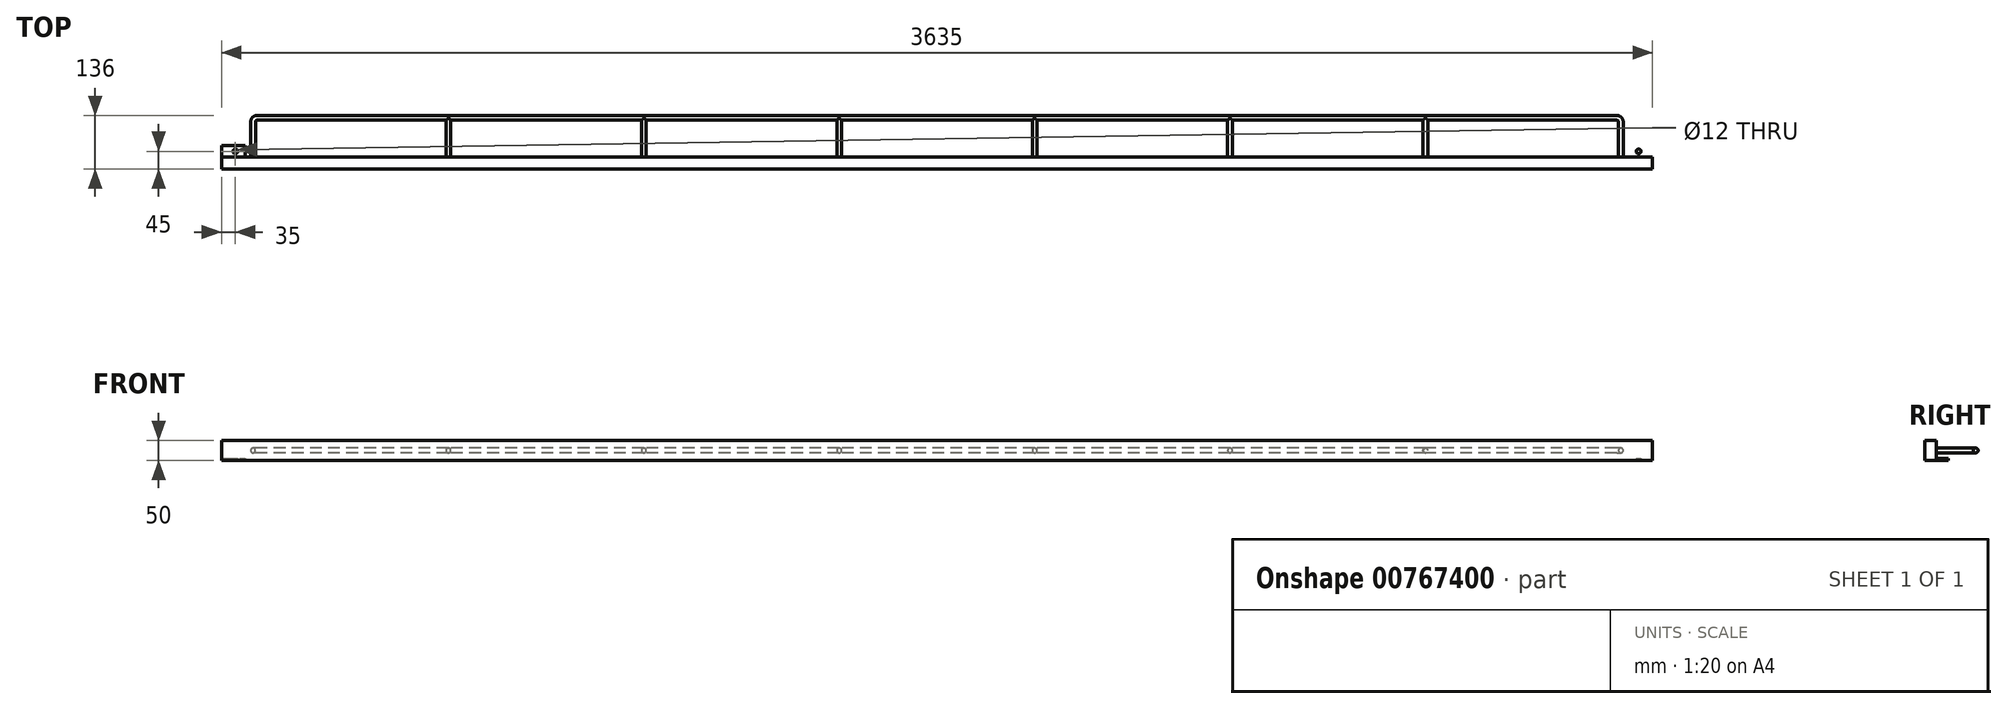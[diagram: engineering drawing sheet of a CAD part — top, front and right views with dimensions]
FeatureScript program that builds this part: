
annotation { "Feature Type Name" : "Feature", "Feature Type Description" : "" }
export const myFeature = defineFeature(function(context is Context, id is Id, definition is map)
    precondition{}
    {
        {
            var Q0;
            Q0=qCreatedBy(makeId("Front.planeOp"),FACE);
            var sketch = newSketch(context, id + "F0", { "sketchPlane" : qUnion([Q0])});
            skLineSegment(sketch, "E0.bottom", {"start": v(1817.5, -25) * mm, "end": v(-1817.5, -25) * mm});
            skLineSegment(sketch, "E0.top", {"start": v(1817.5, 25) * mm, "end": v(-1817.5, 25) * mm});
            skLineSegment(sketch, "E0.left", {"start": v(1817.5, -25) * mm, "end": v(1817.5, 25) * mm});
            skLineSegment(sketch, "E0.right", {"start": v(-1817.5, -25) * mm, "end": v(-1817.5, 25) * mm});
            skPoint(sketch, "E0.middle", {"position": v(0, 0) * mm});
            skSolve(sketch);
        }
        {
            var Q0;
            Q0=qSketchRegion(id+"F0",true);
            extrude(context, id + "F1", {"entities" : qUnion([Q0]), "depth" : 15 * mm, "offsetDistance" : 25 * mm, "hasSecondDirection" : true, "secondDirectionOppositeDirection" : true, "secondDirectionDepth" : 15 * mm});
        }
        {
            var Q0;
            Q0=makeQuery(id+"F1.opExtrude","SWEPT_FACE",FACE,{"disambiguationData":[OSD([sQuery(id+"F0.wireOp",EDGE,"E0.bottom")])]});
            var sketch = newSketch(context, id + "F2", { "sketchPlane" : qUnion([Q0])});
            skLineSegment(sketch, "E1.0", {"start": v(-1817.5, 15) * mm, "end": v(-1817.5, -15) * mm});
            skLineSegment(sketch, "E2.bottom", {"start": v(-1817.5, -15) * mm, "end": v(-1757.5, -15) * mm});
            skLineSegment(sketch, "E2.top", {"start": v(-1817.5, 45) * mm, "end": v(-1757.5, 45) * mm});
            skLineSegment(sketch, "E2.left", {"start": v(-1817.5, -15) * mm, "end": v(-1817.5, 45) * mm});
            skLineSegment(sketch, "E2.right", {"start": v(-1757.5, -15) * mm, "end": v(-1757.5, 45) * mm});
            skLineSegment(sketch, "E3", {"start": v(-1817.5, 0) * mm, "end": v(-1773.05, 0) * mm});
            skLineSegment(sketch, "E4.MirrorCS", {"start": v(-1817.5, -15) * mm, "end": v(-1817.5, 15) * mm});
            skLineSegment(sketch, "E5.MirrorCS", {"start": v(-1817.5, 15) * mm, "end": v(-1817.5, -45) * mm});
            skLineSegment(sketch, "E6.MirrorCS", {"start": v(-1817.5, -45) * mm, "end": v(-1757.5, -45) * mm});
            skLineSegment(sketch, "E7.MirrorCS", {"start": v(-1757.5, 15) * mm, "end": v(-1757.5, -45) * mm});
            skSolve(sketch);
        }
        {
            var Q0;
            {var subQ0=sQuery(id+"F2.wireOp",EDGE,"E2.bottom");Q0=makeQuery(id+"F2.imprint","IMPRINT",FACE,{"disambiguationData":[TD([[makeQuery(id+"F2.imprint","IMPRINT",EDGE,{"derivedFrom":subQ0}),1.0]])]});}
            var Q1;
            {var subQ1=sQuery(id+"F2.wireOp",EDGE,"E2.bottom");Q1=makeQuery(id+"F2.imprint","IMPRINT",FACE,{"disambiguationData":[TD([[makeQuery(id+"F2.imprint","IMPRINT",EDGE,{"derivedFrom":subQ1}),-1.0]])]});}
            extrude(context, id + "F3", {"entities" : qUnion([Q0, Q1]), "operationType" : NewBodyOperationType.ADD, "depth" : 5 * mm, "offsetDistance" : 25 * mm});
        }
        {
            var Q0;
            Q0=makeQuery(id+"F1.opExtrude","SWEPT_FACE",FACE,{"disambiguationData":[OSD([sQuery(id+"F0.wireOp",EDGE,"E0.bottom")])]});
            var sketch = newSketch(context, id + "F4", { "sketchPlane" : qUnion([Q0])});
            skLineSegment(sketch, "E8.0", {"start": v(1817.5, 15) * mm, "end": v(1817.5, -15) * mm});
            skLineSegment(sketch, "E9.bottom", {"start": v(1817.5, -15) * mm, "end": v(1757.5, -15) * mm});
            skLineSegment(sketch, "E9.top", {"start": v(1817.5, 45) * mm, "end": v(1757.5, 45) * mm});
            skLineSegment(sketch, "E9.left", {"start": v(1817.5, -15) * mm, "end": v(1817.5, 45) * mm});
            skLineSegment(sketch, "E9.right", {"start": v(1757.5, -15) * mm, "end": v(1757.5, 45) * mm});
            skLineSegment(sketch, "E10", {"start": v(1817.5, 0) * mm, "end": v(1727.5, 0) * mm});
            skLineSegment(sketch, "E11.MirrorCS", {"start": v(1817.5, 15) * mm, "end": v(1817.5, -45) * mm});
            skLineSegment(sketch, "E12.MirrorCS", {"start": v(1817.5, -45) * mm, "end": v(1757.5, -45) * mm});
            skLineSegment(sketch, "E13.MirrorCS", {"start": v(1757.5, 15) * mm, "end": v(1757.5, -45) * mm});
            skSolve(sketch);
        }
        {
            var Q0;
            {var subQ0=sQuery(id+"F4.wireOp",EDGE,"E9.bottom");Q0=makeQuery(id+"F4.imprint","IMPRINT",FACE,{"disambiguationData":[TD([[makeQuery(id+"F4.imprint","IMPRINT",EDGE,{"derivedFrom":subQ0}),1.0]])]});}
            var Q1;
            {var subQ1=sQuery(id+"F4.wireOp",EDGE,"E9.bottom");Q1=makeQuery(id+"F4.imprint","IMPRINT",FACE,{"disambiguationData":[TD([[makeQuery(id+"F4.imprint","IMPRINT",EDGE,{"derivedFrom":subQ1}),-1.0]])]});}
            var Q2;
            {var subQ0=sQuery(id+"F4.wireOp",EDGE,"E11.MirrorCS");var subQ1=sQuery(id+"F4.wireOp",EDGE,"E10");var subQ2=makeQuery(id+"F4.imprint","INTERSECT",VERTEX,{"derivedFrom":[subQ1,subQ0]});Q2=makeQuery(id+"F4.imprint","IMPRINT",FACE,{"disambiguationData":[TD([[makeQuery(id+"F4.imprint","IMPRINT",EDGE,{"disambiguationData":[TD([[subQ2,-1.0]])],"derivedFrom":subQ1}),-1.0]])]});}
            extrude(context, id + "F5", {"entities" : qUnion([Q0, Q1, Q2]), "operationType" : NewBodyOperationType.ADD, "depth" : 5 * mm, "offsetDistance" : 25 * mm});
        }
        {
            var Q0;
            Q0=makeQuery(id+"F5.opExtrude","CAP_FACE",FACE,{"disambiguationData":[OSD([sQuery(id+"F0.wireOp",EDGE,"E0.bottom"),sQuery(id+"F4.wireOp",EDGE,"E11.MirrorCS"),sQuery(id+"F4.wireOp",EDGE,"E12.MirrorCS"),sQuery(id+"F4.wireOp",EDGE,"E13.MirrorCS")])],"isStart":false});
            var sketch = newSketch(context, id + "F6", { "sketchPlane" : qUnion([Q0])});
            skCircle(sketch, "E14.0", {"center": v(1762.5, 0) * mm, "radius": 6 * mm});
            skCircle(sketch, "E15.0", {"center": v(1722.5, 0) * mm, "radius": 6 * mm});
            skLineSegment(sketch, "E16", {"start": v(1817.5, 15) * mm, "end": v(1817.5, -45) * mm});
            skCircle(sketch, "E17.MirrorC", {"center": v(1782.5, -30) * mm, "radius": 6 * mm});
            skLineSegment(sketch, "E18.0", {"start": v(1817.5, -15) * mm, "end": v(1817.5, -45) * mm});
            skLineSegment(sketch, "E19", {"start": v(1782.5, -30) * mm, "end": v(1817.5, -30) * mm});
            skSolve(sketch);
        }
        {
            var Q0;
            Q0=makeQuery(id+"F6.imprint","IMPRINT",FACE,{"disambiguationData":[TD([[makeQuery(id+"F6.imprint","IMPRINT",EDGE,{"derivedFrom":sQuery(id+"F6.wireOp",EDGE,"E17.MirrorC")}),-1.0]])]});
            var Q1;
            Q1=makeQuery(id+"F6.imprint","IMPRINT",FACE,{"disambiguationData":[TD([[makeQuery(id+"F6.imprint","IMPRINT",EDGE,{"derivedFrom":sQuery(id+"F6.wireOp",EDGE,"f1c2a5ba-6244-45c4-a5ad-aa170d6a38100.MirrorC")}),-1.0]])]});
            var Q2;
            Q2=makeQuery(id+"F5.opExtrude","CAP_FACE",FACE,{"disambiguationData":[OSD([sQuery(id+"F0.wireOp",EDGE,"E0.bottom"),sQuery(id+"F4.wireOp",EDGE,"E11.MirrorCS"),sQuery(id+"F4.wireOp",EDGE,"E12.MirrorCS"),sQuery(id+"F4.wireOp",EDGE,"E13.MirrorCS")])],"isStart":true});
            extrude(context, id + "F7", {"entities" : qUnion([Q0, Q1]), "operationType" : NewBodyOperationType.REMOVE, "endBound" : BoundingType.UP_TO_SURFACE, "oppositeDirection" : true, "depth" : 25 * mm, "endBoundEntityFace" : qUnion([Q2]), "offsetDistance" : 25 * mm});
        }
        {
            var Q0;
            Q0=makeQuery(id+"F3.opExtrude","CAP_FACE",FACE,{"disambiguationData":[OSD([sQuery(id+"F0.wireOp",EDGE,"E0.bottom"),sQuery(id+"F2.wireOp",EDGE,"E5.MirrorCS"),sQuery(id+"F2.wireOp",EDGE,"E6.MirrorCS"),sQuery(id+"F2.wireOp",EDGE,"E7.MirrorCS")])],"isStart":false});
            var sketch = newSketch(context, id + "F8", { "sketchPlane" : qUnion([Q0])});
            skLineSegment(sketch, "E20.bottom", {"start": v(-1817.5, 15) * mm, "end": v(-1792.5, 15) * mm, "construction": true});
            skLineSegment(sketch, "E20.top", {"start": v(-1817.5, 0) * mm, "end": v(-1792.5, 0) * mm});
            skLineSegment(sketch, "E20.left", {"start": v(-1817.5, 15) * mm, "end": v(-1817.5, 0) * mm});
            skLineSegment(sketch, "E20.right", {"start": v(-1792.5, 15) * mm, "end": v(-1792.5, 0) * mm});
            skLineSegment(sketch, "E21", {"start": v(-1792.5, 0) * mm, "end": v(-1752.5, 0) * mm});
            skLineSegment(sketch, "E22", {"start": v(-1757.5, 15) * mm, "end": v(-1757.5, -45) * mm});
            skLineSegment(sketch, "E23", {"start": v(-1757.5, -15) * mm, "end": v(-1776.34, -15) * mm});
            skCircle(sketch, "E24.MirrorC", {"center": v(-1782.5, -30) * mm, "radius": 6 * mm});
            skLineSegment(sketch, "E25", {"start": v(-1782.5, -30) * mm, "end": v(-1817.5, -30) * mm});
            skSolve(sketch);
        }
        {
            var Q0;
            Q0=qSketchRegion(id+"F8",true);
            extrude(context, id + "F9", {"entities" : qUnion([Q0]), "operationType" : NewBodyOperationType.REMOVE, "endBound" : BoundingType.UP_TO_NEXT, "oppositeDirection" : true, "depth" : 25 * mm, "offsetDistance" : 25 * mm});
        }
        {
            var Q0;
            Q0=makeQuery(id+"F5.opExtrude","CAP_FACE",FACE,{"disambiguationData":[OSD([sQuery(id+"F0.wireOp",EDGE,"E0.bottom"),sQuery(id+"F4.wireOp",EDGE,"E11.MirrorCS"),sQuery(id+"F4.wireOp",EDGE,"E12.MirrorCS"),sQuery(id+"F4.wireOp",EDGE,"E13.MirrorCS")])],"isStart":true});
            var Q1;
            Q1=makeQuery(id+"F3.opExtrude","CAP_FACE",FACE,{"disambiguationData":[OSD([sQuery(id+"F0.wireOp",EDGE,"E0.bottom"),sQuery(id+"F2.wireOp",EDGE,"E5.MirrorCS"),sQuery(id+"F2.wireOp",EDGE,"E6.MirrorCS"),sQuery(id+"F2.wireOp",EDGE,"E7.MirrorCS")])],"isStart":true});
            extrude(context, id + "F10", {"entities" : qUnion([Q0, Q1]), "operationType" : NewBodyOperationType.ADD, "depth" : 5 * mm, "offsetDistance" : 25 * mm});
        }
        {
            var Q0;
            Q0=makeQuery(id+"F3.opExtrude","CAP_FACE",FACE,{"disambiguationData":[OSD([sQuery(id+"F0.wireOp",EDGE,"E0.bottom"),sQuery(id+"F2.wireOp",EDGE,"E5.MirrorCS"),sQuery(id+"F2.wireOp",EDGE,"E6.MirrorCS"),sQuery(id+"F2.wireOp",EDGE,"E7.MirrorCS")])],"isStart":false});
            var Q1;
            Q1=makeQuery(id+"F5.opExtrude","CAP_FACE",FACE,{"disambiguationData":[OSD([sQuery(id+"F0.wireOp",EDGE,"E0.bottom"),sQuery(id+"F4.wireOp",EDGE,"E11.MirrorCS"),sQuery(id+"F4.wireOp",EDGE,"E12.MirrorCS"),sQuery(id+"F4.wireOp",EDGE,"E13.MirrorCS")])],"isStart":false});
            extrude(context, id + "F11", {"entities" : qUnion([Q0, Q1]), "operationType" : NewBodyOperationType.REMOVE, "oppositeDirection" : true, "depth" : 5 * mm, "offsetDistance" : 25 * mm});
        }
        {
            var Q0;
            Q0=makeQuery(id+"F1.opExtrude","CAP_FACE",FACE,{"disambiguationData":[OSD([sQuery(id+"F0.wireOp",EDGE,"E0.bottom"),sQuery(id+"F0.wireOp",EDGE,"E0.top"),sQuery(id+"F0.wireOp",EDGE,"E0.left"),sQuery(id+"F0.wireOp",EDGE,"E0.right")])],"isStart":true});
            var sketch = newSketch(context, id + "F12", { "sketchPlane" : qUnion([Q0])});
            skLineSegment(sketch, "E26", {"start": v(-1757.5, -25) * mm, "end": v(-1757.5, 25) * mm, "construction": true});
            skLineSegment(sketch, "E27", {"start": v(1757.5, -25) * mm, "end": v(1757.5, 25) * mm, "construction": true});
            skLineSegment(sketch, "E28", {"start": v(1757.5, -25) * mm, "end": v(1737.5, -25) * mm});
            skLineSegment(sketch, "E29", {"start": v(-1757.5, -25) * mm, "end": v(-1737.5, -25) * mm});
            skLineSegment(sketch, "E30", {"start": v(-1737.5, -25) * mm, "end": v(-1737.5, 0) * mm});
            skPoint(sketch, "E31.orphan", {"position": v(-1757.5, 0) * mm});
            skLineSegment(sketch, "E32", {"start": v(-1737.5, 0) * mm, "end": v(-1241.07, 0) * mm});
            skLineSegment(sketch, "E33", {"start": v(-1241.07, 0) * mm, "end": v(-744.64, 0) * mm});
            skLineSegment(sketch, "E34", {"start": v(-744.64, 0) * mm, "end": v(-248.21, 0) * mm});
            skLineSegment(sketch, "E35", {"start": v(-248.21, 0) * mm, "end": v(248.21, 0) * mm});
            skLineSegment(sketch, "E36", {"start": v(248.21, 0) * mm, "end": v(744.64, 0) * mm});
            skLineSegment(sketch, "E37", {"start": v(744.64, 0) * mm, "end": v(1241.07, 0) * mm});
            skLineSegment(sketch, "E38", {"start": v(1241.07, 0) * mm, "end": v(1737.5, 0) * mm});
            skCircle(sketch, "E39", {"center": v(-1737.5, 0) * mm, "radius": 6 * mm});
            skCircle(sketch, "E40", {"center": v(-1241.07, 0) * mm, "radius": 6 * mm});
            skCircle(sketch, "E41", {"center": v(-744.64, 0) * mm, "radius": 6 * mm});
            skCircle(sketch, "E42", {"center": v(-248.21, 0) * mm, "radius": 6 * mm});
            skCircle(sketch, "E43", {"center": v(248.21, 0) * mm, "radius": 6 * mm});
            skCircle(sketch, "E44", {"center": v(744.64, 0) * mm, "radius": 6 * mm});
            skCircle(sketch, "E45", {"center": v(1241.07, 0) * mm, "radius": 6 * mm});
            skCircle(sketch, "E46", {"center": v(1737.5, 0) * mm, "radius": 6 * mm});
            skSolve(sketch);
        }
        {
            var Q0;
            Q0=qCreatedBy(makeId("Top.planeOp"),FACE);
            var sketch = newSketch(context, id + "F13", { "sketchPlane" : qUnion([Q0])});
            skLineSegment(sketch, "E47", {"start": v(1241.07, 15) * mm, "end": v(1241.07, 115) * mm});
            skLineSegment(sketch, "E48", {"start": v(744.64, 15) * mm, "end": v(744.64, 115) * mm});
            skLineSegment(sketch, "E49", {"start": v(248.21, 15) * mm, "end": v(248.21, 115) * mm});
            skLineSegment(sketch, "E50", {"start": v(-248.21, 115) * mm, "end": v(-248.21, 15) * mm});
            skLineSegment(sketch, "E51", {"start": v(-744.64, 115) * mm, "end": v(-744.64, 15) * mm});
            skLineSegment(sketch, "E52", {"start": v(-1241.07, 115) * mm, "end": v(-1241.07, 15) * mm});
            skLineSegment(sketch, "E53", {"start": v(-1737.5, 105) * mm, "end": v(-1737.5, 15) * mm});
            skLineSegment(sketch, "E54", {"start": v(-1737.5, 105) * mm, "end": v(-1727.5, 105) * mm});
            skArc(sketch, "E55", {"start": v(-1727.5, 115) * mm, "mid": v(-1734.57, 112.07) * mm, "end": v(-1737.5, 105) * mm});
            skLineSegment(sketch, "E56", {"start": v(1727.5, 115) * mm, "end": v(-1727.5, 115) * mm});
            skLineSegment(sketch, "E57", {"start": v(1737.5, 105) * mm, "end": v(1737.5, 15) * mm});
            skLineSegment(sketch, "E58", {"start": v(1727.5, 115) * mm, "end": v(1727.5, 105) * mm});
            skArc(sketch, "E59", {"start": v(1737.5, 105) * mm, "mid": v(1734.57, 112.07) * mm, "end": v(1727.5, 115) * mm});
            skSolve(sketch);
        }
        {
            var Q0;
            {var subQ0=sQuery(id+"F12.wireOp",EDGE,"E32");var subQ1=sQuery(id+"F12.wireOp",EDGE,"E30");var subQ2=makeQuery(id+"F12.imprint","INTERSECT",VERTEX,{"derivedFrom":[subQ1,subQ0]});Q0=makeQuery(id+"F12.imprint","IMPRINT",FACE,{"disambiguationData":[TD([[makeQuery(id+"F12.imprint","IMPRINT",EDGE,{"disambiguationData":[TD([[subQ2,1.0]])],"derivedFrom":subQ1}),1.0]])]});}
            var Q1;
            {var subQ0=sQuery(id+"F12.wireOp",EDGE,"E32");var subQ1=sQuery(id+"F12.wireOp",EDGE,"E30");var subQ2=makeQuery(id+"F12.imprint","INTERSECT",VERTEX,{"derivedFrom":[subQ1,subQ0]});Q1=makeQuery(id+"F12.imprint","IMPRINT",FACE,{"disambiguationData":[TD([[makeQuery(id+"F12.imprint","IMPRINT",EDGE,{"disambiguationData":[TD([[subQ2,1.0]])],"derivedFrom":subQ1}),-1.0]])]});}
            var Q2;
            Q2=sQuery(id+"F13.wireOp",EDGE,"E57");
            var Q3;
            Q3=sQuery(id+"F13.wireOp",EDGE,"E59");
            var Q4;
            Q4=sQuery(id+"F13.wireOp",EDGE,"E56");
            var Q5;
            Q5=sQuery(id+"F13.wireOp",EDGE,"E55");
            var Q6;
            Q6=sQuery(id+"F13.wireOp",EDGE,"E53");
            sweep(context, id + "F14", {"operationType" : NewBodyOperationType.ADD, "profiles" : qUnion([Q0, Q1]), "path" : qUnion([Q2, Q3, Q4, Q5, Q6])});
        }
        {
            var Q0;
            {var subQ0=sQuery(id+"F12.wireOp",EDGE,"E38");var subQ1=sQuery(id+"F12.wireOp",EDGE,"E37");var subQ2=makeQuery(id+"F12.imprint","INTERSECT",VERTEX,{"derivedFrom":[subQ1,subQ0]});Q0=makeQuery(id+"F12.imprint","IMPRINT",FACE,{"disambiguationData":[TD([[makeQuery(id+"F12.imprint","IMPRINT",EDGE,{"disambiguationData":[TD([[subQ2,1.0]])],"derivedFrom":subQ1}),1.0]])]});}
            var Q1;
            {var subQ0=sQuery(id+"F12.wireOp",EDGE,"E38");var subQ1=sQuery(id+"F12.wireOp",EDGE,"E37");var subQ2=makeQuery(id+"F12.imprint","INTERSECT",VERTEX,{"derivedFrom":[subQ1,subQ0]});Q1=makeQuery(id+"F12.imprint","IMPRINT",FACE,{"disambiguationData":[TD([[makeQuery(id+"F12.imprint","IMPRINT",EDGE,{"disambiguationData":[TD([[subQ2,1.0]])],"derivedFrom":subQ1}),-1.0]])]});}
            var Q2;
            Q2=sQuery(id+"F13.wireOp",EDGE,"E52");
            sweep(context, id + "F15", {"operationType" : NewBodyOperationType.ADD, "profiles" : qUnion([Q0, Q1]), "path" : qUnion([Q2])});
        }
        {
            var Q0;
            {var subQ0=sQuery(id+"F12.wireOp",EDGE,"E37");var subQ1=sQuery(id+"F12.wireOp",EDGE,"E36");var subQ2=makeQuery(id+"F12.imprint","INTERSECT",VERTEX,{"derivedFrom":[subQ1,subQ0]});Q0=makeQuery(id+"F12.imprint","IMPRINT",FACE,{"disambiguationData":[TD([[makeQuery(id+"F12.imprint","IMPRINT",EDGE,{"disambiguationData":[TD([[subQ2,1.0]])],"derivedFrom":subQ1}),1.0]])]});}
            var Q1;
            {var subQ0=sQuery(id+"F12.wireOp",EDGE,"E37");var subQ1=sQuery(id+"F12.wireOp",EDGE,"E36");var subQ2=makeQuery(id+"F12.imprint","INTERSECT",VERTEX,{"derivedFrom":[subQ1,subQ0]});Q1=makeQuery(id+"F12.imprint","IMPRINT",FACE,{"disambiguationData":[TD([[makeQuery(id+"F12.imprint","IMPRINT",EDGE,{"disambiguationData":[TD([[subQ2,1.0]])],"derivedFrom":subQ1}),-1.0]])]});}
            var Q2;
            Q2=sQuery(id+"F13.wireOp",EDGE,"E51");
            sweep(context, id + "F16", {"operationType" : NewBodyOperationType.ADD, "profiles" : qUnion([Q0, Q1]), "path" : qUnion([Q2])});
        }
        {
            var Q0;
            {var subQ0=sQuery(id+"F12.wireOp",EDGE,"E36");var subQ1=sQuery(id+"F12.wireOp",EDGE,"E35");var subQ2=makeQuery(id+"F12.imprint","INTERSECT",VERTEX,{"derivedFrom":[subQ1,subQ0]});Q0=makeQuery(id+"F12.imprint","IMPRINT",FACE,{"disambiguationData":[TD([[makeQuery(id+"F12.imprint","IMPRINT",EDGE,{"disambiguationData":[TD([[subQ2,1.0]])],"derivedFrom":subQ1}),1.0]])]});}
            var Q1;
            {var subQ0=sQuery(id+"F12.wireOp",EDGE,"E36");var subQ1=sQuery(id+"F12.wireOp",EDGE,"E35");var subQ2=makeQuery(id+"F12.imprint","INTERSECT",VERTEX,{"derivedFrom":[subQ1,subQ0]});Q1=makeQuery(id+"F12.imprint","IMPRINT",FACE,{"disambiguationData":[TD([[makeQuery(id+"F12.imprint","IMPRINT",EDGE,{"disambiguationData":[TD([[subQ2,1.0]])],"derivedFrom":subQ1}),-1.0]])]});}
            var Q2;
            Q2=sQuery(id+"F13.wireOp",EDGE,"E50");
            sweep(context, id + "F17", {"operationType" : NewBodyOperationType.ADD, "profiles" : qUnion([Q0, Q1]), "path" : qUnion([Q2])});
        }
        {
            var Q0;
            {var subQ0=sQuery(id+"F12.wireOp",EDGE,"E35");var subQ1=sQuery(id+"F12.wireOp",EDGE,"E34");var subQ2=makeQuery(id+"F12.imprint","INTERSECT",VERTEX,{"derivedFrom":[subQ1,subQ0]});Q0=makeQuery(id+"F12.imprint","IMPRINT",FACE,{"disambiguationData":[TD([[makeQuery(id+"F12.imprint","IMPRINT",EDGE,{"disambiguationData":[TD([[subQ2,1.0]])],"derivedFrom":subQ1}),1.0]])]});}
            var Q1;
            {var subQ0=sQuery(id+"F12.wireOp",EDGE,"E35");var subQ1=sQuery(id+"F12.wireOp",EDGE,"E34");var subQ2=makeQuery(id+"F12.imprint","INTERSECT",VERTEX,{"derivedFrom":[subQ1,subQ0]});Q1=makeQuery(id+"F12.imprint","IMPRINT",FACE,{"disambiguationData":[TD([[makeQuery(id+"F12.imprint","IMPRINT",EDGE,{"disambiguationData":[TD([[subQ2,1.0]])],"derivedFrom":subQ1}),-1.0]])]});}
            var Q2;
            Q2=sQuery(id+"F13.wireOp",EDGE,"E49");
            sweep(context, id + "F18", {"operationType" : NewBodyOperationType.ADD, "profiles" : qUnion([Q0, Q1]), "path" : qUnion([Q2])});
        }
        {
            var Q0;
            {var subQ0=sQuery(id+"F12.wireOp",EDGE,"E34");var subQ1=sQuery(id+"F12.wireOp",EDGE,"E33");var subQ2=makeQuery(id+"F12.imprint","INTERSECT",VERTEX,{"derivedFrom":[subQ1,subQ0]});Q0=makeQuery(id+"F12.imprint","IMPRINT",FACE,{"disambiguationData":[TD([[makeQuery(id+"F12.imprint","IMPRINT",EDGE,{"disambiguationData":[TD([[subQ2,1.0]])],"derivedFrom":subQ1}),1.0]])]});}
            var Q1;
            {var subQ0=sQuery(id+"F12.wireOp",EDGE,"E34");var subQ1=sQuery(id+"F12.wireOp",EDGE,"E33");var subQ2=makeQuery(id+"F12.imprint","INTERSECT",VERTEX,{"derivedFrom":[subQ1,subQ0]});Q1=makeQuery(id+"F12.imprint","IMPRINT",FACE,{"disambiguationData":[TD([[makeQuery(id+"F12.imprint","IMPRINT",EDGE,{"disambiguationData":[TD([[subQ2,1.0]])],"derivedFrom":subQ1}),-1.0]])]});}
            var Q2;
            Q2=sQuery(id+"F13.wireOp",EDGE,"E48");
            sweep(context, id + "F19", {"operationType" : NewBodyOperationType.ADD, "profiles" : qUnion([Q0, Q1]), "path" : qUnion([Q2])});
        }
        {
            var Q0;
            {var subQ0=sQuery(id+"F12.wireOp",EDGE,"E33");var subQ1=sQuery(id+"F12.wireOp",EDGE,"E32");var subQ2=makeQuery(id+"F12.imprint","INTERSECT",VERTEX,{"derivedFrom":[subQ1,subQ0]});Q0=makeQuery(id+"F12.imprint","IMPRINT",FACE,{"disambiguationData":[TD([[makeQuery(id+"F12.imprint","IMPRINT",EDGE,{"disambiguationData":[TD([[subQ2,1.0]])],"derivedFrom":subQ1}),1.0]])]});}
            var Q1;
            {var subQ0=sQuery(id+"F12.wireOp",EDGE,"E33");var subQ1=sQuery(id+"F12.wireOp",EDGE,"E32");var subQ2=makeQuery(id+"F12.imprint","INTERSECT",VERTEX,{"derivedFrom":[subQ1,subQ0]});Q1=makeQuery(id+"F12.imprint","IMPRINT",FACE,{"disambiguationData":[TD([[makeQuery(id+"F12.imprint","IMPRINT",EDGE,{"disambiguationData":[TD([[subQ2,1.0]])],"derivedFrom":subQ1}),-1.0]])]});}
            var Q2;
            Q2=sQuery(id+"F13.wireOp",EDGE,"E47");
            sweep(context, id + "F20", {"operationType" : NewBodyOperationType.ADD, "profiles" : qUnion([Q0, Q1]), "path" : qUnion([Q2])});
        }
    });
